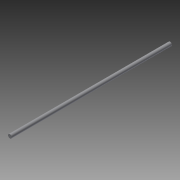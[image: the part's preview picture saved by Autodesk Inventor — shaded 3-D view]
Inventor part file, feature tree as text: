
AUTODESK INVENTOR PART (.ipt)
format: ipt  version: 2015 SP2 (Build 190223200, 223)  size: 65,536 bytes
history: native  units: mm
features: extrude x1, sketch x1
ambient origin geometry x8: Origin, YZ Plane, XZ Plane, XY Plane, X Axis, Y Axis, Z Axis, Center Point
bodies: Solid1 (feature_tree)
feature tree (2):
  extrude  "Extrusion1"  Depth=340.0mm TaperAngle=0.0deg
  sketch  "Sketch1"  dims[d0=8.0mm d1=340.0mm d2=0.0mm]
